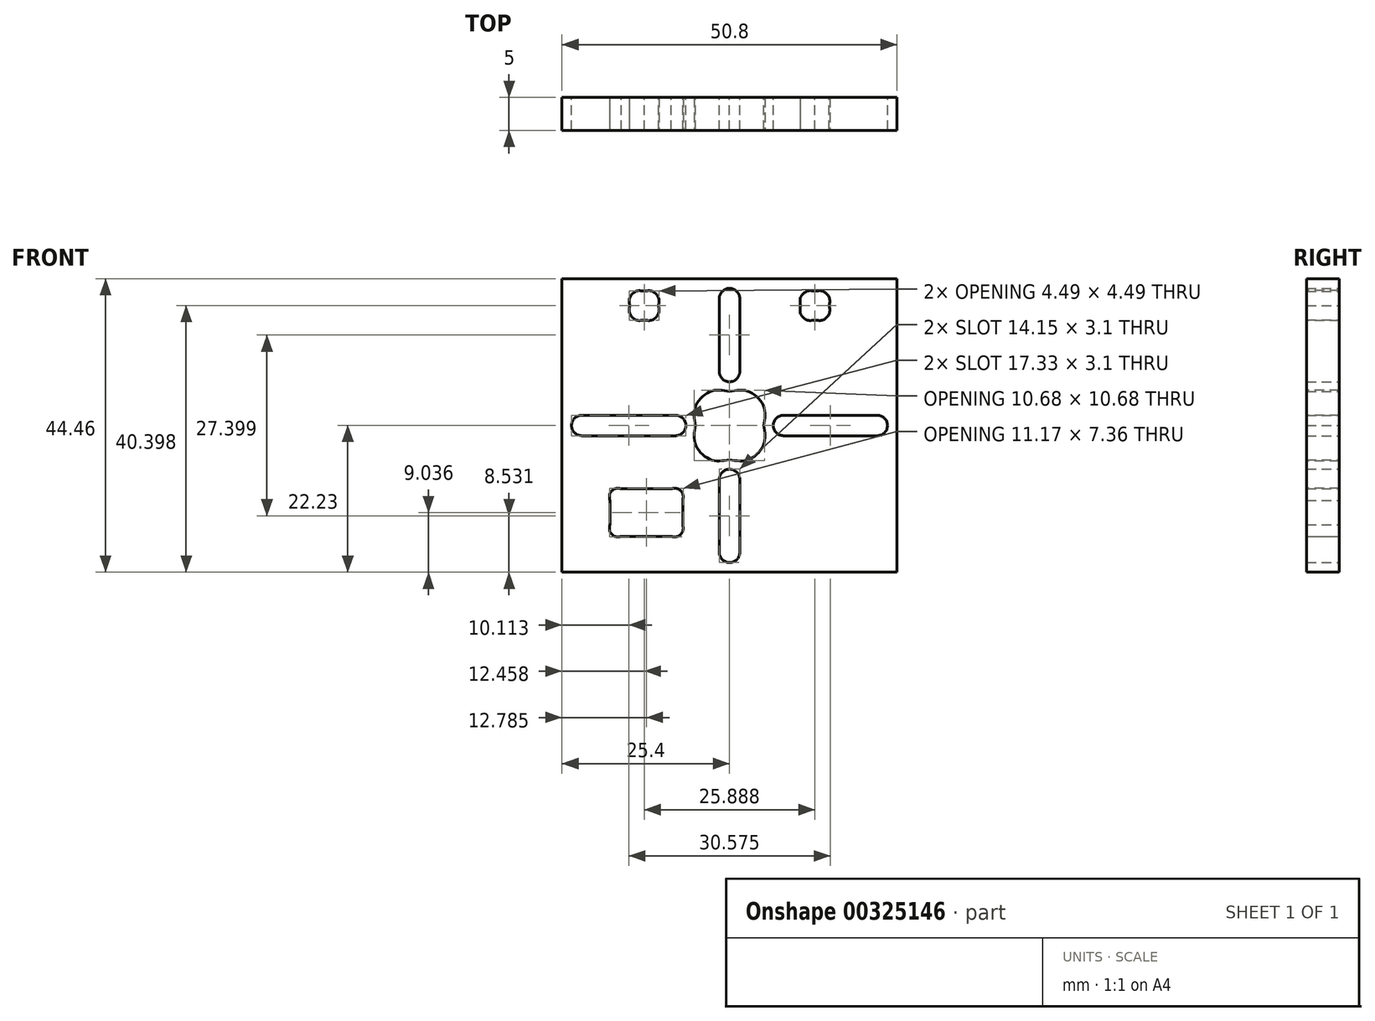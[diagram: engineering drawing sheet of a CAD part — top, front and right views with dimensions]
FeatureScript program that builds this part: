
annotation { "Feature Type Name" : "Feature", "Feature Type Description" : "" }
export const myFeature = defineFeature(function(context is Context, id is Id, definition is map)
    precondition{}
    {
        {
            var Q0;
            Q0=qCreatedBy(makeId("Front.planeOp"),FACE);
            var sketch = newSketch(context, id + "F0", { "sketchPlane" : qUnion([Q0])});
            skFitSpline(sketch, "E0", {"points": [v(-7.09, -11.34) * mm, v(-7.09, -10.36) * mm, v(-7.88, -9.57) * mm, v(-8.85, -9.57) * mm]});
            skFitSpline(sketch, "E1", {"points": [v(-16.38, -9.57) * mm, v(-17.35, -9.57) * mm, v(-18.14, -10.36) * mm, v(-18.14, -11.34) * mm]});
            skLineSegment(sketch, "E2", {"start": v(-8.85, -9.57) * mm, "end": v(-16.38, -9.57) * mm});
            skFitSpline(sketch, "E3", {"points": [v(-18.14, -15.05) * mm, v(-18.14, -16.03) * mm, v(-17.35, -16.82) * mm, v(-16.38, -16.82) * mm]});
            skLineSegment(sketch, "E4", {"start": v(-18.14, -11.34) * mm, "end": v(-18.14, -15.05) * mm});
            skFitSpline(sketch, "E5", {"points": [v(-8.85, -16.82) * mm, v(-7.88, -16.82) * mm, v(-7.09, -16.03) * mm, v(-7.09, -15.05) * mm]});
            skLineSegment(sketch, "E6", {"start": v(-16.38, -16.82) * mm, "end": v(-8.85, -16.82) * mm});
            skFitSpline(sketch, "E7", {"points": [v(0, 5.17) * mm, v(-2.86, 5.17) * mm, v(-5.17, 2.86) * mm, v(-5.17, 0) * mm]});
            skFitSpline(sketch, "E8", {"points": [v(-5.17, 0) * mm, v(-5.17, -2.86) * mm, v(-2.86, -5.17) * mm, v(0, -5.17) * mm]});
            skFitSpline(sketch, "E9", {"points": [v(0, -5.17) * mm, v(2.86, -5.17) * mm, v(5.17, -2.86) * mm, v(5.17, 0) * mm]});
            skFitSpline(sketch, "E10", {"points": [v(5.17, 0) * mm, v(5.17, 2.86) * mm, v(2.86, 5.17) * mm, v(0, 5.17) * mm]});
            skLineSegment(sketch, "E11", {"start": v(-7.09, -15.05) * mm, "end": v(-7.09, -11.34) * mm});
            skFitSpline(sketch, "E12", {"points": [v(12.95, 20.34) * mm, v(11.74, 20.34) * mm, v(10.77, 19.37) * mm, v(10.77, 18.17) * mm]});
            skFitSpline(sketch, "E13", {"points": [v(10.77, 18.17) * mm, v(10.77, 16.97) * mm, v(11.74, 16) * mm, v(12.95, 16) * mm]});
            skFitSpline(sketch, "E14", {"points": [v(12.95, 16) * mm, v(14.15, 16) * mm, v(15.12, 16.97) * mm, v(15.12, 18.17) * mm]});
            skFitSpline(sketch, "E15", {"points": [v(15.12, 18.17) * mm, v(15.12, 19.37) * mm, v(14.15, 20.34) * mm, v(12.95, 20.34) * mm]});
            skFitSpline(sketch, "E16", {"points": [v(-12.94, 20.34) * mm, v(-14.14, 20.34) * mm, v(-15.12, 19.37) * mm, v(-15.12, 18.17) * mm]});
            skFitSpline(sketch, "E17", {"points": [v(-15.12, 18.17) * mm, v(-15.12, 16.97) * mm, v(-14.14, 16) * mm, v(-12.94, 16) * mm]});
            skFitSpline(sketch, "E18", {"points": [v(-12.94, 16) * mm, v(-11.74, 16) * mm, v(-10.77, 16.97) * mm, v(-10.77, 18.17) * mm]});
            skFitSpline(sketch, "E19", {"points": [v(-10.77, 18.17) * mm, v(-10.77, 19.37) * mm, v(-11.74, 20.34) * mm, v(-12.94, 20.34) * mm]});
            skLineSegment(sketch, "E20", {"start": v(25.4, 22.23) * mm, "end": v(-25.4, 22.23) * mm});
            skLineSegment(sketch, "E21", {"start": v(-25.4, 22.23) * mm, "end": v(-25.4, -22.22) * mm});
            skLineSegment(sketch, "E22", {"start": v(-25.4, -22.22) * mm, "end": v(25.4, -22.22) * mm});
            skLineSegment(sketch, "E23", {"start": v(25.4, 22.23) * mm, "end": v(25.4, -22.22) * mm});
            skLineSegment(sketch, "E24", {"start": v(-5.17, 0) * mm, "end": v(-8.17, 0) * mm, "construction": true});
            skLineSegment(sketch, "E25", {"start": v(-22.4, 0) * mm, "end": v(-25.4, 0) * mm, "construction": true});
            skLineSegment(sketch, "E26", {"start": v(-8.17, 1.55) * mm, "end": v(-22.4, 1.55) * mm});
            skLineSegment(sketch, "E27", {"start": v(-22.4, -1.55) * mm, "end": v(-8.17, -1.55) * mm});
            skArc(sketch, "E28", {"start": v(-22.4, 1.55) * mm, "mid": v(-23.95, 0) * mm, "end": v(-22.4, -1.55) * mm});
            skArc(sketch, "E29", {"start": v(-8.17, -1.55) * mm, "mid": v(-6.62, 0) * mm, "end": v(-8.17, 1.55) * mm});
            skArc(sketch, "E30.MirrorCS", {"start": v(22.4, 1.55) * mm, "mid": v(23.95, 0) * mm, "end": v(22.4, -1.55) * mm});
            skLineSegment(sketch, "E31.MirrorCS", {"start": v(8.17, 1.55) * mm, "end": v(22.4, 1.55) * mm});
            skLineSegment(sketch, "E32.MirrorCS", {"start": v(22.4, -1.55) * mm, "end": v(8.17, -1.55) * mm});
            skArc(sketch, "E33.MirrorCS", {"start": v(8.17, -1.55) * mm, "mid": v(6.62, 0) * mm, "end": v(8.17, 1.55) * mm});
            skLineSegment(sketch, "E34", {"start": v(0, 22.23) * mm, "end": v(0, 19.23) * mm, "construction": true});
            skLineSegment(sketch, "E35", {"start": v(0, 5.17) * mm, "end": v(0, 8.17) * mm, "construction": true});
            skLineSegment(sketch, "E36", {"start": v(-1.55, 19.23) * mm, "end": v(-1.55, 19.23) * mm});
            skLineSegment(sketch, "E37", {"start": v(1.55, 19.23) * mm, "end": v(1.55, 19.22) * mm});
            skLineSegment(sketch, "E38", {"start": v(-1.55, 19.23) * mm, "end": v(-1.55, 8.17) * mm});
            skLineSegment(sketch, "E39", {"start": v(1.55, 19.22) * mm, "end": v(1.55, 8.17) * mm});
            skArc(sketch, "E40", {"start": v(-1.55, 8.19) * mm, "mid": v(0, 6.62) * mm, "end": v(1.55, 8.17) * mm});
            skArc(sketch, "E41", {"start": v(1.55, 19.22) * mm, "mid": v(0, 20.77) * mm, "end": v(-1.55, 19.23) * mm});
            skArc(sketch, "E42.MirrorCS", {"start": v(-1.55, -8.19) * mm, "mid": v(0, -6.62) * mm, "end": v(1.55, -8.17) * mm});
            skLineSegment(sketch, "E43.MirrorCS", {"start": v(-1.55, -19.23) * mm, "end": v(-1.55, -8.17) * mm});
            skLineSegment(sketch, "E44.MirrorCS", {"start": v(1.55, -19.22) * mm, "end": v(1.55, -8.17) * mm});
            skArc(sketch, "E45.MirrorCS", {"start": v(1.55, -19.22) * mm, "mid": v(0, -20.77) * mm, "end": v(-1.55, -19.23) * mm});
            skSolve(sketch);
        }
        {
            var Q0;
            Q0=makeQuery(id+"F0.imprint","IMPRINT",FACE,{"disambiguationData":[TD([[makeQuery(id+"F0.imprint","IMPRINT",EDGE,{"derivedFrom":sQuery(id+"F0.wireOp",EDGE,"E0")}),-1.0]])]});
            extrude(context, id + "F1", {"entities" : qUnion([Q0]), "depth" : 5 * mm});
        }
    });
